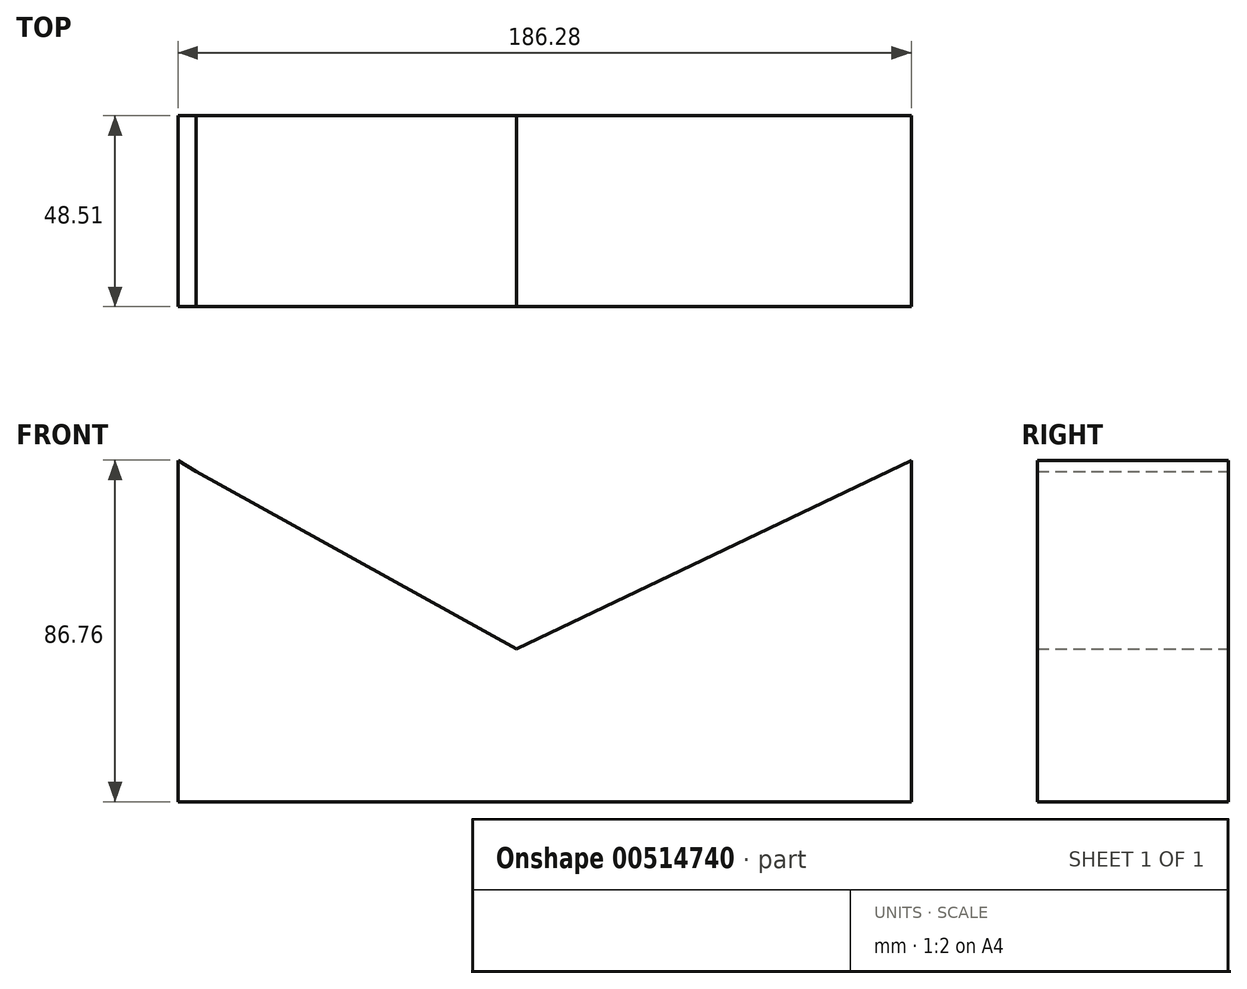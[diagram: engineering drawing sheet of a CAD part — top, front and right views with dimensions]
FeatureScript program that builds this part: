
annotation { "Feature Type Name" : "Feature", "Feature Type Description" : "" }
export const myFeature = defineFeature(function(context is Context, id is Id, definition is map)
    precondition{}
    {
        {
            var Q0;
            Q0=qCreatedBy(makeId("Front.planeOp"),FACE);
            var sketch = newSketch(context, id + "F0", { "sketchPlane" : qUnion([Q0])});
            skLineSegment(sketch, "E0.bottom", {"start": v(-86.03, 38.08) * mm, "end": v(100.25, 38.08) * mm});
            skLineSegment(sketch, "E0.top", {"start": v(-86.03, -48.68) * mm, "end": v(100.25, -48.68) * mm});
            skLineSegment(sketch, "E0.left", {"start": v(-86.03, 38.08) * mm, "end": v(-86.03, -48.68) * mm});
            skLineSegment(sketch, "E0.right", {"start": v(100.25, 38.08) * mm, "end": v(100.25, -48.68) * mm});
            skLineSegment(sketch, "E1", {"start": v(-86.03, 38.08) * mm, "end": v(-81.46, 35.19) * mm});
            skLineSegment(sketch, "E2", {"start": v(-81.46, 35.19) * mm, "end": v(0, -9.88) * mm});
            skLineSegment(sketch, "E3", {"start": v(0, -9.88) * mm, "end": v(100.25, 38.08) * mm});
            skSolve(sketch);
        }
        {
            var Q0;
            Q0=makeQuery(id+"F0.imprint","IMPRINT",FACE,{"disambiguationData":[TD([[makeQuery(id+"F0.imprint","IMPRINT",EDGE,{"derivedFrom":sQuery(id+"F0.wireOp",EDGE,"E0.top")}),1.0]])]});
            extrude(context, id + "F1", {"entities" : qUnion([Q0]), "depth" : 48.5 * mm, "offsetDistance" : 25.4 * mm});
        }
    });
